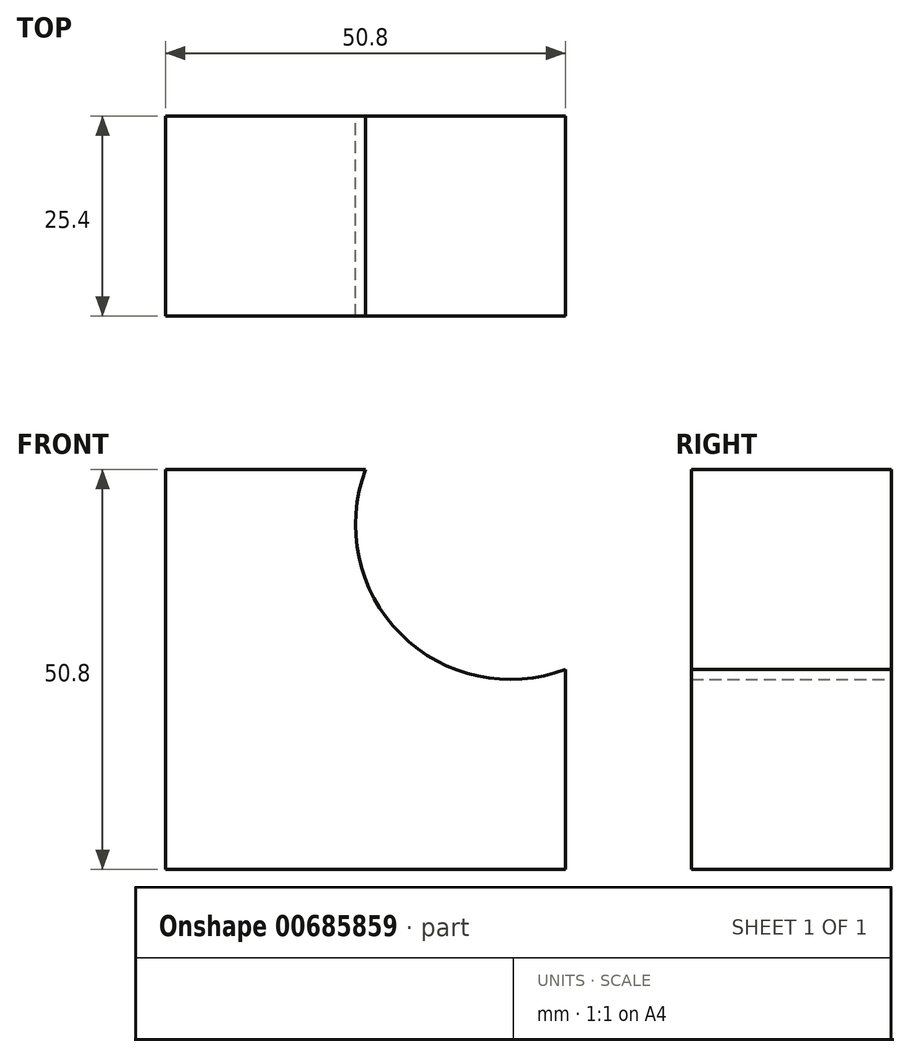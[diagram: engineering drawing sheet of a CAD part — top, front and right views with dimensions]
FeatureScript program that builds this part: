
annotation { "Feature Type Name" : "Feature", "Feature Type Description" : "" }
export const myFeature = defineFeature(function(context is Context, id is Id, definition is map)
    precondition{}
    {
        {
            var Q0;
            Q0=qCreatedBy(makeId("Front.planeOp"),FACE);
            var sketch = newSketch(context, id + "F0", { "sketchPlane" : qUnion([Q0])});
            skLineSegment(sketch, "E0", {"start": v(-25.4, 25.4) * mm, "end": v(-25.4, -25.4) * mm});
            skLineSegment(sketch, "E1", {"start": v(-25.4, -25.4) * mm, "end": v(25.4, -25.4) * mm});
            skLineSegment(sketch, "E2", {"start": v(-25.4, 25.4) * mm, "end": v(0, 25.4) * mm});
            skLineSegment(sketch, "E3", {"start": v(25.4, -25.4) * mm, "end": v(25.4, 0) * mm});
            skArc(sketch, "E4", {"start": v(0, 25.4) * mm, "mid": v(4.49, 4.49) * mm, "end": v(25.4, 0) * mm});
            skSolve(sketch);
        }
        {
            var Q0;
            Q0 = qSketchRegion(id + "F0", true);
            extrude(context, id + "F1", {"entities" : qUnion([Q0]), "depth" : 25.4 * mm, "offsetDistance" : 25.4 * mm});
        }
    });
